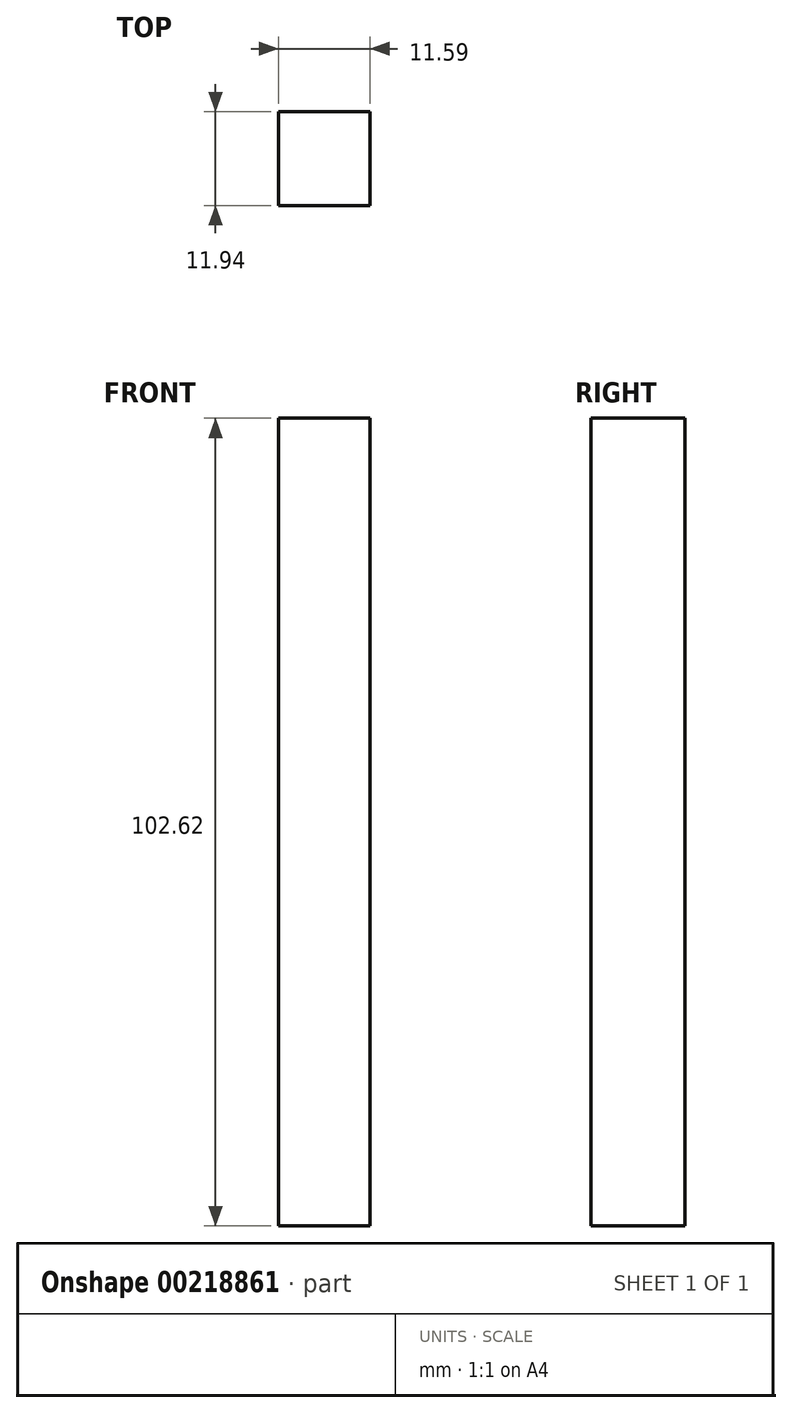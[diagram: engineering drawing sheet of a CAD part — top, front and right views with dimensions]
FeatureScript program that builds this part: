
annotation { "Feature Type Name" : "Feature", "Feature Type Description" : "" }
export const myFeature = defineFeature(function(context is Context, id is Id, definition is map)
    precondition{}
    {
        {
            var Q0;
            Q0=qCreatedBy(makeId("Top.planeOp"),FACE);
            var sketch = newSketch(context, id + "F0", { "sketchPlane" : qUnion([Q0])});
            skLineSegment(sketch, "E0.bottom", {"start": v(0, 0) * mm, "end": v(11.59, 0) * mm});
            skLineSegment(sketch, "E0.top", {"start": v(0, 11.94) * mm, "end": v(11.59, 11.94) * mm});
            skLineSegment(sketch, "E0.left", {"start": v(0, 0) * mm, "end": v(0, 11.94) * mm});
            skLineSegment(sketch, "E0.right", {"start": v(11.59, 0) * mm, "end": v(11.59, 11.94) * mm});
            skSolve(sketch);
        }
        {
            var Q0;
            Q0=makeQuery(id+"F0.imprint","IMPRINT",FACE,{"disambiguationData":[TD([[makeQuery(id+"F0.imprint","IMPRINT",EDGE,{"derivedFrom":sQuery(id+"F0.wireOp",EDGE,"E0.bottom")}),1.0]])]});
            var sketch = newSketch(context, id + "F1", { "sketchPlane" : qUnion([Q0])});
            skSolve(sketch);
        }
        {
            var Q0;
            Q0 = qSketchRegion(id + "F1", true);
            var Q1;
            Q1=makeQuery(id+"F0.imprint","IMPRINT",FACE,{"disambiguationData":[TD([[makeQuery(id+"F0.imprint","IMPRINT",EDGE,{"derivedFrom":sQuery(id+"F0.wireOp",EDGE,"E0.bottom")}),1.0]])]});
            extrude(context, id + "F2", {"entities" : qUnion([Q0, Q1]), "depth" : 102.62 * mm});
        }
    });
